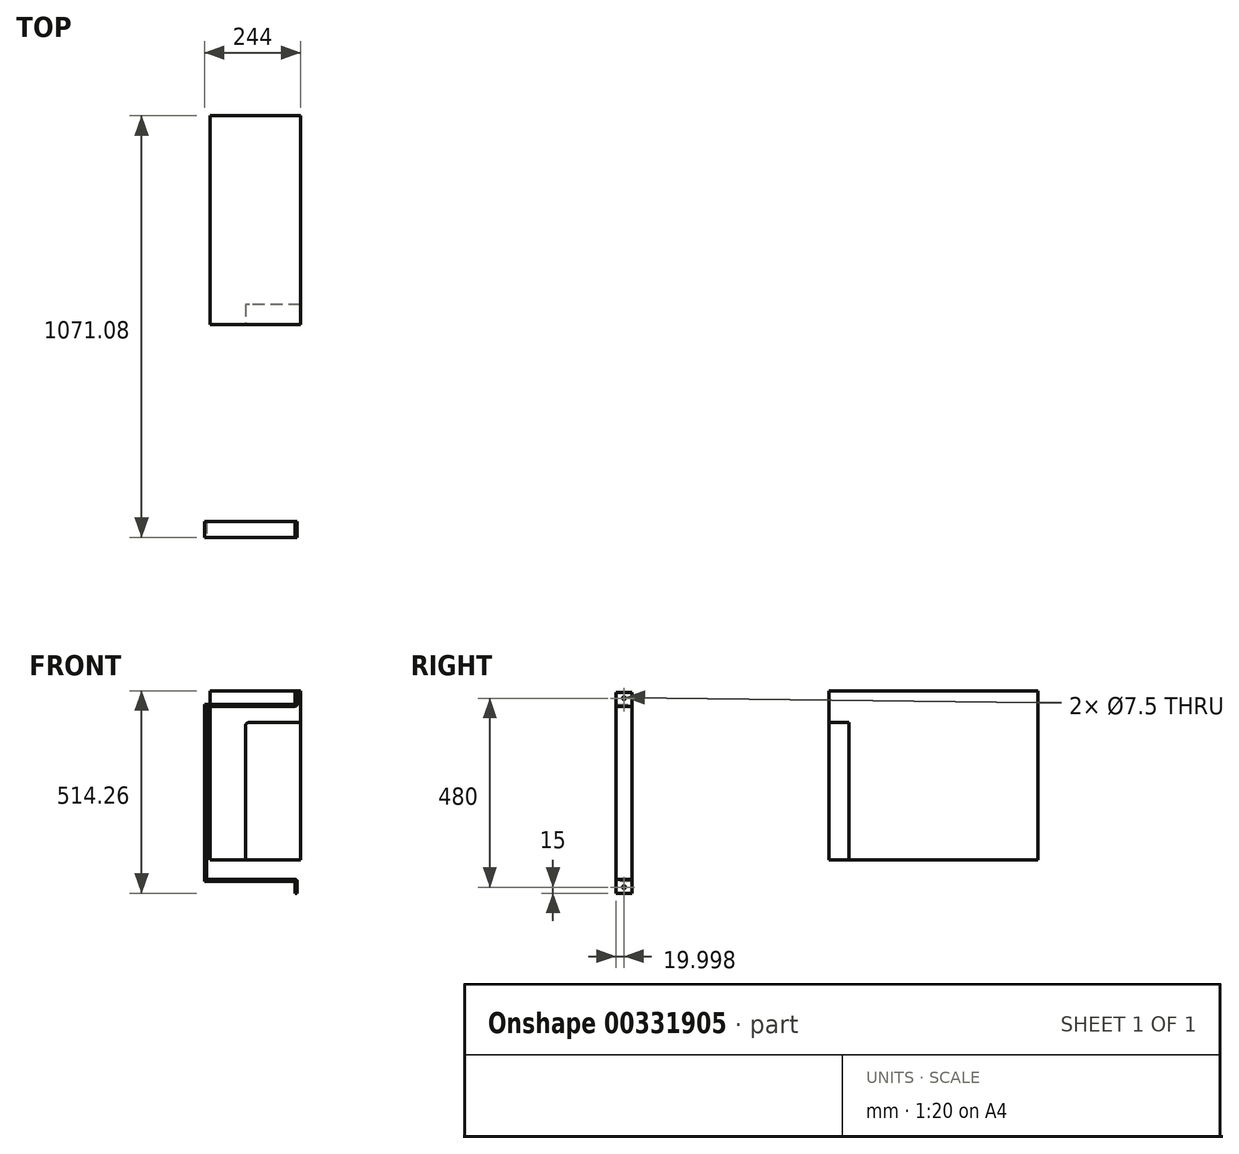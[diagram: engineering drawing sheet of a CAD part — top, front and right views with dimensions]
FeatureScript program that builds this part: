
annotation { "Feature Type Name" : "Feature", "Feature Type Description" : "" }
export const myFeature = defineFeature(function(context is Context, id is Id, definition is map)
    precondition{}
    {
        {
            var Q0;
            Q0=qCreatedBy(makeId("Front.planeOp"),FACE);
            var sketch = newSketch(context, id + "F0", { "sketchPlane" : qUnion([Q0])});
            skLineSegment(sketch, "E0.bottom", {"start": v(115, 215) * mm, "end": v(-115, 215) * mm});
            skLineSegment(sketch, "E0.top", {"start": v(115, -215) * mm, "end": v(-115, -215) * mm});
            skLineSegment(sketch, "E0.left", {"start": v(115, 215) * mm, "end": v(115, -215) * mm});
            skLineSegment(sketch, "E0.right", {"start": v(-115, 215) * mm, "end": v(-115, -215) * mm});
            skPoint(sketch, "E0.middle", {"position": v(0, 0) * mm});
            skSolve(sketch);
        }
        {
            var Q0;
            Q0=makeQuery(id+"F0.imprint","IMPRINT",FACE,{"disambiguationData":[TD([[makeQuery(id+"F0.imprint","IMPRINT",EDGE,{"derivedFrom":sQuery(id+"F0.wireOp",EDGE,"E0.bottom")}),1.0]])]});
            var sketch = newSketch(context, id + "F1", { "sketchPlane" : qUnion([Q0])});
            skLineSegment(sketch, "E1.bottom", {"start": v(115, -215) * mm, "end": v(-25, -215) * mm});
            skLineSegment(sketch, "E1.top", {"start": v(115, 135) * mm, "end": v(-25, 135) * mm});
            skLineSegment(sketch, "E1.left", {"start": v(115, -215) * mm, "end": v(115, 135) * mm});
            skLineSegment(sketch, "E1.right", {"start": v(-25, -215) * mm, "end": v(-25, 135) * mm});
            skSolve(sketch);
        }
        {
            var Q0;
            Q0=makeQuery(id+"F0.imprint","IMPRINT",FACE,{"disambiguationData":[TD([[makeQuery(id+"F0.imprint","IMPRINT",EDGE,{"derivedFrom":sQuery(id+"F0.wireOp",EDGE,"E0.bottom")}),1.0]])]});
            extrude(context, id + "F2", {"entities" : qUnion([Q0]), "oppositeDirection" : true, "depth" : 530 * mm});
        }
        {
            var Q0;
            Q0 = qSketchRegion(id + "F1", true);
            var Q1;
            Q1=makeQuery(id+"F1.imprint","IMPRINT",FACE,{"disambiguationData":[TD([[makeQuery(id+"F1.imprint","IMPRINT",EDGE,{"derivedFrom":sQuery(id+"F1.wireOp",EDGE,"E1.bottom")}),-1.0]])]});
            extrude(context, id + "F3", {"entities" : qUnion([Q0, Q1]), "operationType" : NewBodyOperationType.REMOVE, "oppositeDirection" : true, "depth" : 50 * mm});
        }
        {
            var Q0;
            Q0=makeQuery(id+"F3.boolean.opBoolean","COPY",EDGE,{"derivedFrom":makeQuery(id+"F3.opExtrude","SWEPT_EDGE",EDGE,{"disambiguationData":[OSD([sQuery(id+"F1.wireOp",EDGE,"E1.top"),sQuery(id+"F1.wireOp",EDGE,"E1.right")])]})});
            fillet(context, id + "F4", {"entities" : qUnion([Q0]), "radius" : 10 * mm, "tangentPropagation" : true, "allowEdgeOverflow" : false});
        }
        {
            var Q0;
            Q0=qCreatedBy(makeId("Right.planeOp"),FACE);
            var sketch = newSketch(context, id + "F5", { "sketchPlane" : qUnion([Q0])});
            skLineSegment(sketch, "E2.bottom", {"start": v(-52.08, -221.26) * mm, "end": v(-92.08, -221.26) * mm});
            skLineSegment(sketch, "E2.top", {"start": v(-52.08, 228.74) * mm, "end": v(-92.08, 228.74) * mm});
            skLineSegment(sketch, "E2.left", {"start": v(-52.08, -221.26) * mm, "end": v(-52.08, 228.74) * mm});
            skLineSegment(sketch, "E2.right", {"start": v(-92.08, -221.26) * mm, "end": v(-92.08, 228.74) * mm});
            skSolve(sketch);
        }
        {
            var Q0;
            Q0=makeQuery(id+"F5.imprint","IMPRINT",FACE,{"disambiguationData":[TD([[makeQuery(id+"F5.imprint","IMPRINT",EDGE,{"derivedFrom":sQuery(id+"F5.wireOp",EDGE,"E2.bottom")}),-1.0]])]});
            extrude(context, id + "F6", {"entities" : qUnion([Q0]), "depth" : 5 * mm});
        }
        {
            var Q0;
            Q0=makeQuery(id+"F6.opExtrude","SWEPT_BODY",BODY,{"disambiguationData":[OSD([sQuery(id+"F5.wireOp",EDGE,"E2.bottom"),sQuery(id+"F5.wireOp",EDGE,"E2.top"),sQuery(id+"F5.wireOp",EDGE,"E2.left"),sQuery(id+"F5.wireOp",EDGE,"E2.right")])]});
            transform(context, id + "F7", {"entities" : qUnion([Q0]), "transformType" : TransformType.TRANSLATION_3D, "dx" : -129 * mm, "dy" : -449 * mm, "dz" : -48 * mm, "makeCopy" : false});
        }
        {
            var Q0;
            Q0=makeQuery(id+"F6.opExtrude","CAP_FACE",FACE,{"disambiguationData":[OSD([sQuery(id+"F5.wireOp",EDGE,"E2.bottom"),sQuery(id+"F5.wireOp",EDGE,"E2.top"),sQuery(id+"F5.wireOp",EDGE,"E2.left"),sQuery(id+"F5.wireOp",EDGE,"E2.right")])],"isStart":false});
            var sketch = newSketch(context, id + "F8", { "sketchPlane" : qUnion([Q0])});
            skLineSegment(sketch, "E3.bottom", {"start": v(-501.08, -269.26) * mm, "end": v(-541.08, -269.26) * mm});
            skLineSegment(sketch, "E3.top", {"start": v(-501.08, -264.26) * mm, "end": v(-541.08, -264.26) * mm});
            skLineSegment(sketch, "E3.left", {"start": v(-501.08, -269.26) * mm, "end": v(-501.08, -264.26) * mm});
            skLineSegment(sketch, "E3.right", {"start": v(-541.08, -269.26) * mm, "end": v(-541.08, -264.26) * mm});
            skLineSegment(sketch, "E4.bottom", {"start": v(-501.08, 180.74) * mm, "end": v(-541.08, 180.74) * mm});
            skLineSegment(sketch, "E4.top", {"start": v(-501.08, 175.74) * mm, "end": v(-541.08, 175.74) * mm});
            skLineSegment(sketch, "E4.left", {"start": v(-501.08, 180.74) * mm, "end": v(-501.08, 175.74) * mm});
            skLineSegment(sketch, "E4.right", {"start": v(-541.08, 180.74) * mm, "end": v(-541.08, 175.74) * mm});
            skSolve(sketch);
        }
        {
            var Q0;
            Q0=makeQuery(id+"F8.imprint","IMPRINT",FACE,{"disambiguationData":[TD([[makeQuery(id+"F8.imprint","IMPRINT",EDGE,{"derivedFrom":sQuery(id+"F8.wireOp",EDGE,"E3.bottom")}),-1.0]])]});
            var Q1;
            Q1=makeQuery(id+"F8.imprint","IMPRINT",FACE,{"disambiguationData":[TD([[makeQuery(id+"F8.imprint","IMPRINT",EDGE,{"derivedFrom":sQuery(id+"F8.wireOp",EDGE,"E4.bottom")}),1.0]])]});
            extrude(context, id + "F9", {"entities" : qUnion([Q0, Q1]), "operationType" : NewBodyOperationType.ADD, "depth" : 230 * mm});
        }
        {
            var Q0;
            Q0=makeQuery(id+"F9.boolean.opBoolean","MERGE",FACE,{"derivedFrom":[makeQuery(id+"F6.opExtrude","SWEPT_FACE",FACE,{"disambiguationData":[OSD([sQuery(id+"F5.wireOp",EDGE,"E2.bottom")])]}),makeQuery(id+"F9.opExtrude","SWEPT_FACE",FACE,{"disambiguationData":[OSD([sQuery(id+"F8.wireOp",EDGE,"E3.bottom")])]})]});
            var sketch = newSketch(context, id + "F10", { "sketchPlane" : qUnion([Q0])});
            skLineSegment(sketch, "E5.bottom", {"start": v(106, 501.08) * mm, "end": v(101, 501.08) * mm});
            skLineSegment(sketch, "E5.top", {"start": v(106, 541.08) * mm, "end": v(101, 541.08) * mm});
            skLineSegment(sketch, "E5.left", {"start": v(106, 501.08) * mm, "end": v(106, 541.08) * mm});
            skLineSegment(sketch, "E5.right", {"start": v(101, 501.08) * mm, "end": v(101, 541.08) * mm});
            skSolve(sketch);
        }
        {
            var Q0;
            Q0=makeQuery(id+"F9.boolean.opBoolean","MERGE",FACE,{"derivedFrom":[makeQuery(id+"F6.opExtrude","SWEPT_FACE",FACE,{"disambiguationData":[OSD([sQuery(id+"F5.wireOp",EDGE,"E2.top")])]}),makeQuery(id+"F9.opExtrude","SWEPT_FACE",FACE,{"disambiguationData":[OSD([sQuery(id+"F8.wireOp",EDGE,"E4.bottom")])]})]});
            var sketch = newSketch(context, id + "F11", { "sketchPlane" : qUnion([Q0])});
            skLineSegment(sketch, "E6.bottom", {"start": v(106, -541.08) * mm, "end": v(101, -541.08) * mm});
            skLineSegment(sketch, "E6.top", {"start": v(106, -501.08) * mm, "end": v(101, -501.08) * mm});
            skLineSegment(sketch, "E6.left", {"start": v(106, -541.08) * mm, "end": v(106, -501.08) * mm});
            skLineSegment(sketch, "E6.right", {"start": v(101, -541.08) * mm, "end": v(101, -501.08) * mm});
            skSolve(sketch);
        }
        {
            var Q0;
            Q0=makeQuery(id+"F10.imprint","IMPRINT",FACE,{"disambiguationData":[TD([[makeQuery(id+"F10.imprint","IMPRINT",EDGE,{"derivedFrom":sQuery(id+"F10.wireOp",EDGE,"E5.bottom")}),-1.0]])]});
            extrude(context, id + "F12", {"entities" : qUnion([Q0]), "operationType" : NewBodyOperationType.ADD, "depth" : 30 * mm});
        }
        {
            var Q0;
            Q0=makeQuery(id+"F11.imprint","IMPRINT",FACE,{"disambiguationData":[TD([[makeQuery(id+"F11.imprint","IMPRINT",EDGE,{"derivedFrom":sQuery(id+"F11.wireOp",EDGE,"E6.bottom")}),-1.0]])]});
            extrude(context, id + "F13", {"entities" : qUnion([Q0]), "operationType" : NewBodyOperationType.ADD, "depth" : 30 * mm});
        }
        {
            var Q0;
            Q0=makeQuery(id+"F9.opExtrude","CAP_EDGE",EDGE,{"disambiguationData":[OSD([sQuery(id+"F8.wireOp",EDGE,"E3.top")])],"isStart":true});
            var Q1;
            Q1=makeQuery(id+"F12.opExtrude","CAP_EDGE",EDGE,{"disambiguationData":[OSD([sQuery(id+"F10.wireOp",EDGE,"E5.right")])],"isStart":true});
            var Q2;
            Q2=makeQuery(id+"F9.opExtrude","CAP_EDGE",EDGE,{"disambiguationData":[OSD([sQuery(id+"F8.wireOp",EDGE,"E4.top")])],"isStart":true});
            var Q3;
            Q3=makeQuery(id+"F13.opExtrude","CAP_EDGE",EDGE,{"disambiguationData":[OSD([sQuery(id+"F11.wireOp",EDGE,"E6.right")])],"isStart":true});
            var Q4;
            Q4=makeQuery(id+"F9.opExtrude","CAP_EDGE",EDGE,{"disambiguationData":[OSD([sQuery(id+"F8.wireOp",EDGE,"E3.top")])],"isStart":false});
            var Q5;
            Q5=makeQuery(id+"F9.opExtrude","CAP_EDGE",EDGE,{"disambiguationData":[OSD([sQuery(id+"F8.wireOp",EDGE,"E4.top")])],"isStart":false});
            fillet(context, id + "F14", {"entities" : qUnion([Q0, Q1, Q2, Q3, Q4, Q5]), "radius" : 5 * mm, "tangentPropagation" : true, "allowEdgeOverflow" : false});
        }
        {
            var Q0;
            Q0=makeQuery(id+"F12.opExtrude","SWEPT_FACE",FACE,{"disambiguationData":[OSD([sQuery(id+"F10.wireOp",EDGE,"E5.right")])]});
            var sketch = newSketch(context, id + "F15", { "sketchPlane" : qUnion([Q0])});
            skCircle(sketch, "E7", {"center": v(521.08, -284.26) * mm, "radius": 3.75 * mm});
            skSolve(sketch);
        }
        {
            var Q0;
            Q0=makeQuery(id+"F13.opExtrude","SWEPT_FACE",FACE,{"disambiguationData":[OSD([sQuery(id+"F11.wireOp",EDGE,"E6.right")])]});
            var sketch = newSketch(context, id + "F16", { "sketchPlane" : qUnion([Q0])});
            skCircle(sketch, "E8", {"center": v(521.08, 195.74) * mm, "radius": 3.75 * mm});
            skSolve(sketch);
        }
        {
            var Q0;
            Q0=makeQuery(id+"F15.imprint","IMPRINT",FACE,{"disambiguationData":[TD([[makeQuery(id+"F15.imprint","IMPRINT",EDGE,{"derivedFrom":sQuery(id+"F15.wireOp",EDGE,"E7")}),1.0]])]});
            extrude(context, id + "F17", {"entities" : qUnion([Q0]), "operationType" : NewBodyOperationType.REMOVE, "oppositeDirection" : true, "depth" : 25 * mm});
        }
        {
            var Q0;
            Q0=makeQuery(id+"F16.imprint","IMPRINT",FACE,{"disambiguationData":[TD([[makeQuery(id+"F16.imprint","IMPRINT",EDGE,{"derivedFrom":sQuery(id+"F16.wireOp",EDGE,"E8")}),1.0]])]});
            extrude(context, id + "F18", {"entities" : qUnion([Q0]), "operationType" : NewBodyOperationType.REMOVE, "oppositeDirection" : true, "depth" : 25 * mm});
        }
    });
